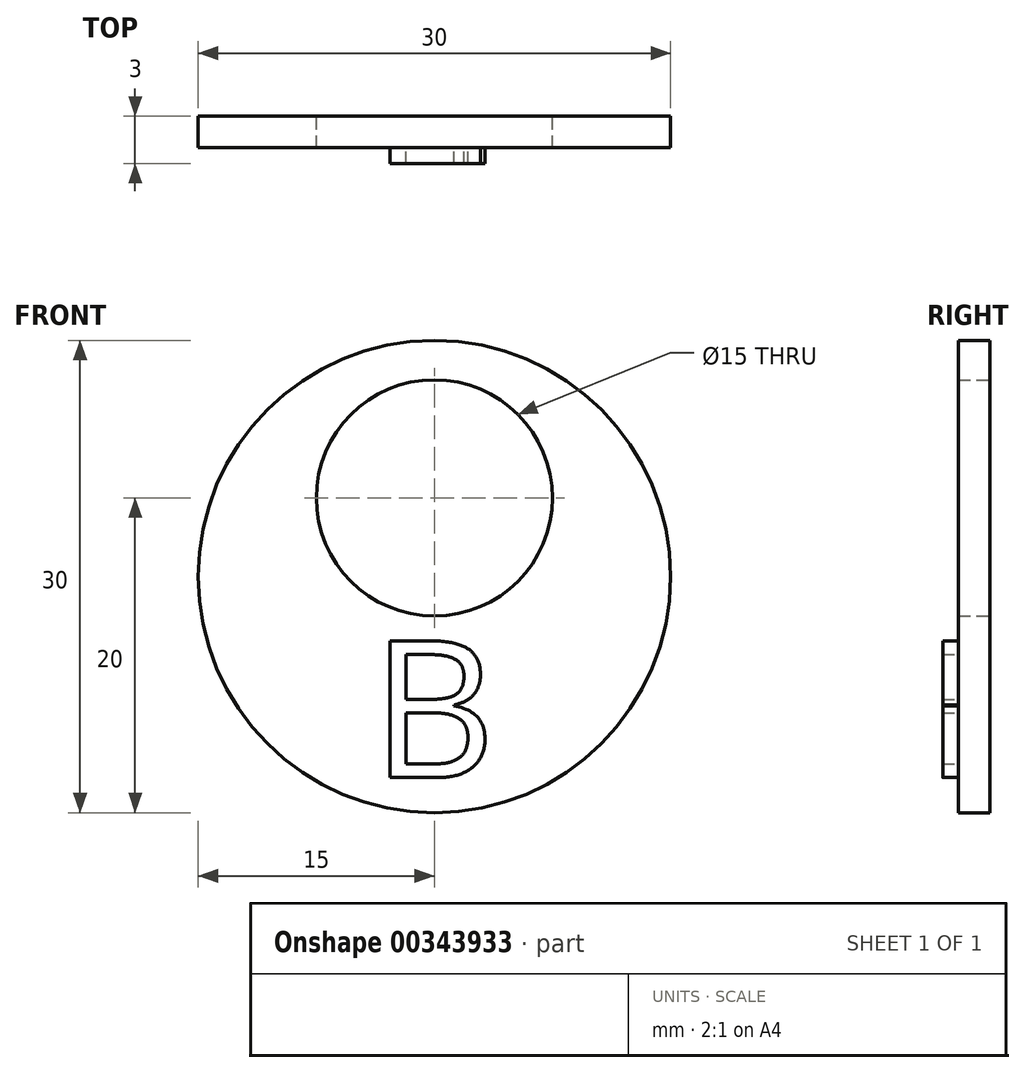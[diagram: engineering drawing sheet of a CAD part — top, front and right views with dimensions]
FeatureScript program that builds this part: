
annotation { "Feature Type Name" : "Feature", "Feature Type Description" : "" }
export const myFeature = defineFeature(function(context is Context, id is Id, definition is map)
    precondition{}
    {
        {
            var Q0;
            Q0=qCreatedBy(makeId("Front.planeOp"),FACE);
            var sketch = newSketch(context, id + "F0", { "sketchPlane" : qUnion([Q0])});
            skCircle(sketch, "E0", {"center": v(0, 0) * mm, "radius": 15 * mm});
            skPoint(sketch, "E1", {"position": v(0, 5) * mm});
            skCircle(sketch, "E2", {"center": v(0, 5) * mm, "radius": 7.5 * mm});
            skSolve(sketch);
        }
        {
            var Q0;
            Q0=makeQuery(id+"F0.imprint","IMPRINT",FACE,{"disambiguationData":[TD([[makeQuery(id+"F0.imprint","IMPRINT",EDGE,{"derivedFrom":sQuery(id+"F0.wireOp",EDGE,"E0")}),1.0]])]});
            extrude(context, id + "F1", {"entities" : qUnion([Q0]), "depth" : 2 * mm});
        }
        {
            var Q0;
            Q0=makeQuery(id+"F1.opExtrude","CAP_FACE",FACE,{"disambiguationData":[OSD([sQuery(id+"F0.wireOp",EDGE,"E0"),sQuery(id+"F0.wireOp",EDGE,"E2")])],"isStart":false});
            var sketch = newSketch(context, id + "F2", { "sketchPlane" : qUnion([Q0])});
            skText(sketch, "E3", { "text": "B", "fontName": "OpenSans-Regular.ttf"});
            const initialGuessF2  = {"E3": [-0.004, -0.01276, 1, 0, 0.00876]};
            skSetInitialGuess(sketch, initialGuessF2);
            skSolve(sketch);
        }
        {
            var Q0;
            Q0 = qSketchRegion(id + "F2", true);
            extrude(context, id + "F3", {"entities" : qUnion([Q0]), "operationType" : NewBodyOperationType.ADD, "depth" : 1 * mm});
        }
    });
